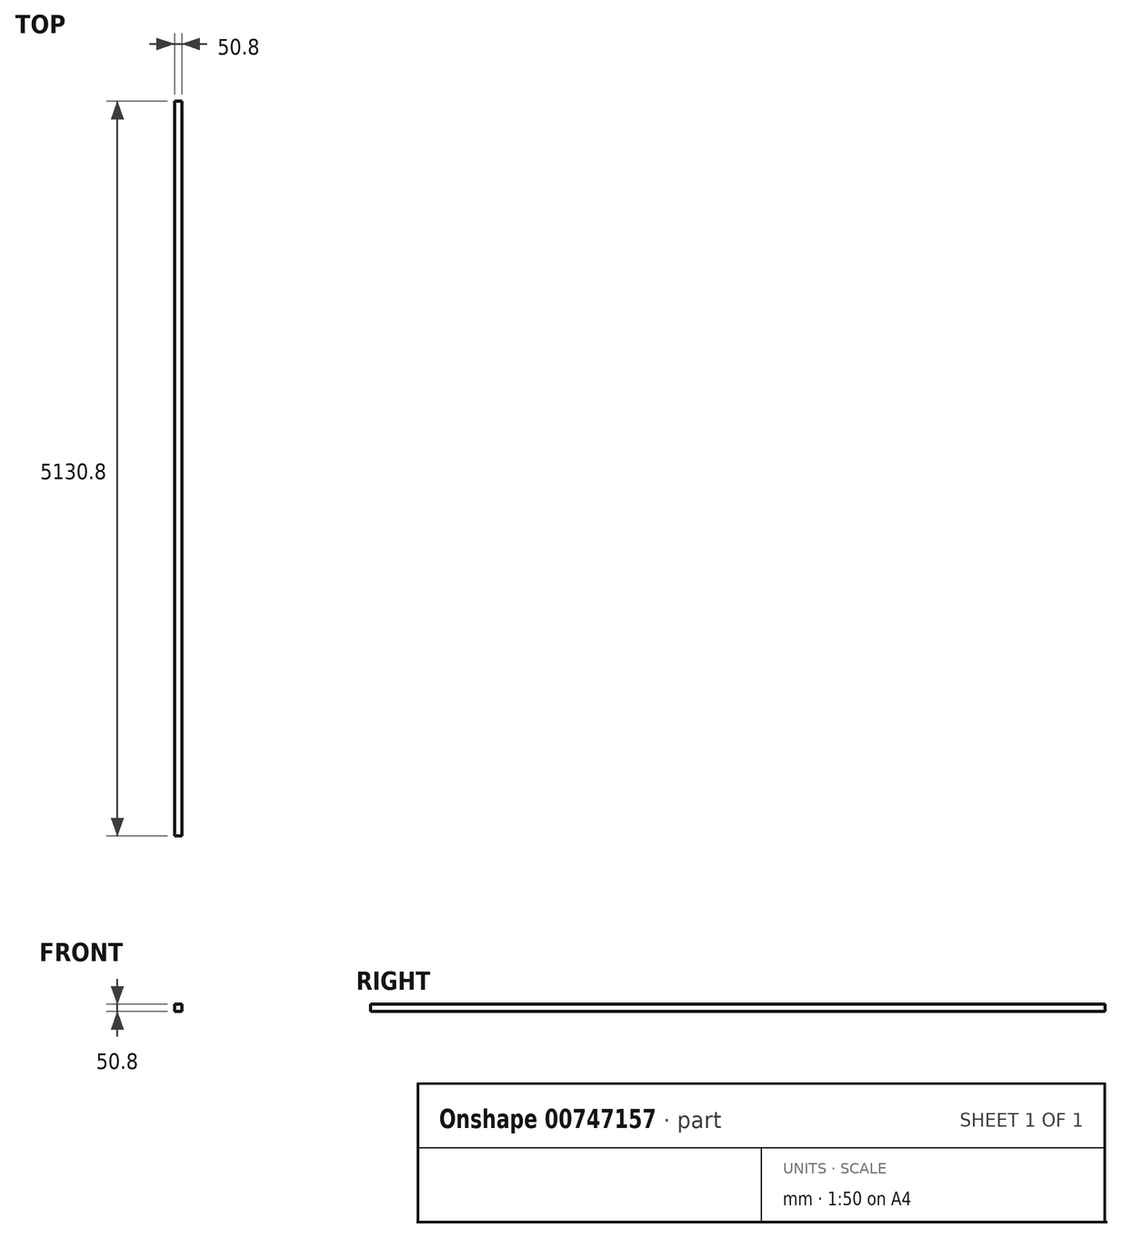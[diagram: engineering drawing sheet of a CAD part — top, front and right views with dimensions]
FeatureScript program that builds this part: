
annotation { "Feature Type Name" : "Feature", "Feature Type Description" : "" }
export const myFeature = defineFeature(function(context is Context, id is Id, definition is map)
    precondition{}
    {
        {
            var Q0;
            Q0=qCreatedBy(makeId("Front.planeOp"),FACE);
            var sketch = newSketch(context, id + "F0", { "sketchPlane" : qUnion([Q0])});
            skLineSegment(sketch, "E0.bottom", {"start": v(-87.98, 59.6) * mm, "end": v(-37.18, 59.6) * mm});
            skLineSegment(sketch, "E0.top", {"start": v(-87.98, 8.8) * mm, "end": v(-37.18, 8.8) * mm});
            skLineSegment(sketch, "E0.left", {"start": v(-87.98, 59.6) * mm, "end": v(-87.98, 8.8) * mm});
            skLineSegment(sketch, "E0.right", {"start": v(-37.18, 59.6) * mm, "end": v(-37.18, 8.8) * mm});
            skSolve(sketch);
        }
        {
            var Q0;
            Q0 = qSketchRegion(id + "F0", true);
            extrude(context, id + "F1", {"entities" : qUnion([Q0]), "depth" : 5130.8 * mm, "offsetDistance" : 25.4 * mm});
        }
    });
